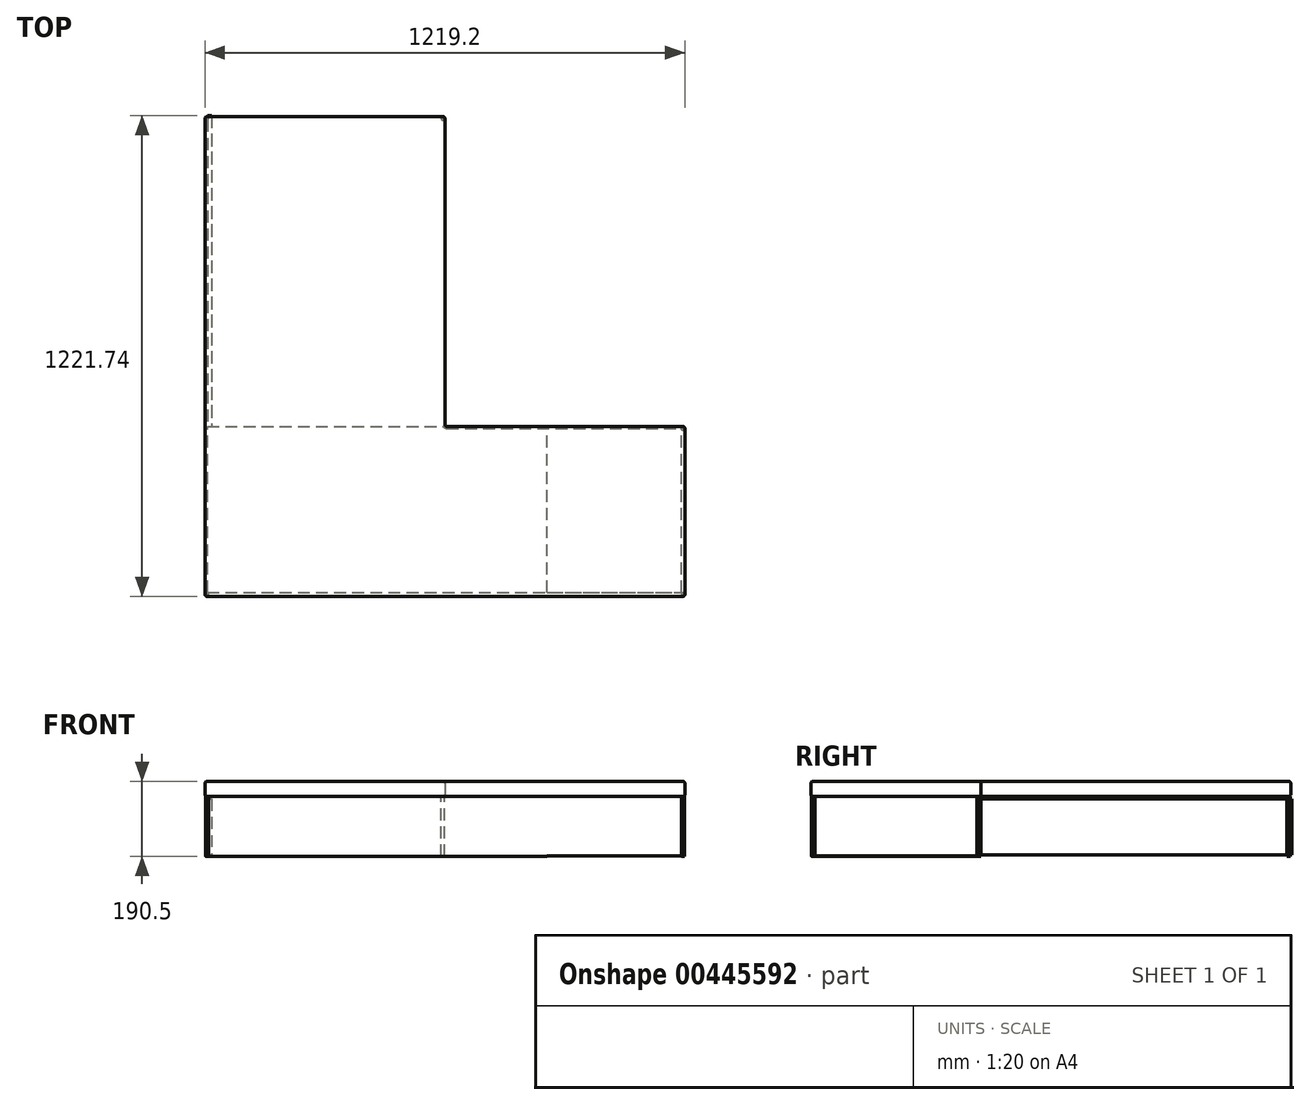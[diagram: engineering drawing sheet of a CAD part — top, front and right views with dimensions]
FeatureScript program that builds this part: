
annotation { "Feature Type Name" : "Feature", "Feature Type Description" : "" }
export const myFeature = defineFeature(function(context is Context, id is Id, definition is map)
    precondition{}
    {
        {
            var Q0;
            Q0=qCreatedBy(makeId("Top.planeOp"),FACE);
            var sketch = newSketch(context, id + "F0", { "sketchPlane" : qUnion([Q0])});
            skLineSegment(sketch, "E0.bottom", {"start": v(0, 0) * mm, "end": v(-609.6, 0) * mm});
            skLineSegment(sketch, "E0.top", {"start": v(0, 787.4) * mm, "end": v(-609.6, 787.4) * mm});
            skLineSegment(sketch, "E0.left", {"start": v(0, 0) * mm, "end": v(0, 787.4) * mm});
            skLineSegment(sketch, "E0.right", {"start": v(-609.6, 0) * mm, "end": v(-609.6, 787.4) * mm});
            skLineSegment(sketch, "E1.top", {"start": v(0, -431.8) * mm, "end": v(-609.6, -431.8) * mm});
            skLineSegment(sketch, "E1.left", {"start": v(0, 0) * mm, "end": v(0, -431.8) * mm});
            skLineSegment(sketch, "E1.right", {"start": v(-609.6, 0) * mm, "end": v(-609.6, -431.8) * mm});
            skLineSegment(sketch, "E2.bottom", {"start": v(0, -431.8) * mm, "end": v(609.6, -431.8) * mm});
            skLineSegment(sketch, "E2.top", {"start": v(0, 0) * mm, "end": v(609.6, 0) * mm});
            skLineSegment(sketch, "E2.left", {"start": v(0, -431.8) * mm, "end": v(0, 0) * mm});
            skLineSegment(sketch, "E2.right", {"start": v(609.6, -431.8) * mm, "end": v(609.6, 0) * mm});
            skSolve(sketch);
        }
        {
            var Q0;
            Q0 = qSketchRegion(id + "F0", true);
            extrude(context, id + "F1", {"entities" : qUnion([Q0]), "depth" : 38.1 * mm});
        }
        {
            var Q0;
            Q0=makeQuery(id+"F1.opExtrude","CAP_EDGE",EDGE,{"disambiguationData":[OSD([sQuery(id+"F0.wireOp",EDGE,"E1.top"),sQuery(id+"F0.wireOp",EDGE,"E2.bottom")])],"isStart":false});
            var Q1;
            Q1=makeQuery(id+"F1.opExtrude","SWEPT_EDGE",EDGE,{"disambiguationData":[OSD([sQuery(id+"F0.wireOp",EDGE,"E2.bottom"),sQuery(id+"F0.wireOp",EDGE,"E2.right")])]});
            var Q2;
            Q2=makeQuery(id+"F1.opExtrude","CAP_EDGE",EDGE,{"disambiguationData":[OSD([sQuery(id+"F0.wireOp",EDGE,"E2.right")])],"isStart":false});
            var Q3;
            Q3=makeQuery(id+"F1.opExtrude","CAP_EDGE",EDGE,{"disambiguationData":[OSD([sQuery(id+"F0.wireOp",EDGE,"E2.top")])],"isStart":false});
            var Q4;
            Q4=makeQuery(id+"F1.opExtrude","CAP_EDGE",EDGE,{"disambiguationData":[OSD([sQuery(id+"F0.wireOp",EDGE,"E0.left")])],"isStart":false});
            var Q5;
            Q5=makeQuery(id+"F1.opExtrude","CAP_EDGE",EDGE,{"disambiguationData":[OSD([sQuery(id+"F0.wireOp",EDGE,"E0.right"),sQuery(id+"F0.wireOp",EDGE,"E1.right")])],"isStart":false});
            var Q6;
            Q6=makeQuery(id+"F1.opExtrude","CAP_EDGE",EDGE,{"disambiguationData":[OSD([sQuery(id+"F0.wireOp",EDGE,"E0.top")])],"isStart":false});
            var Q7;
            Q7=makeQuery(id+"F1.opExtrude","CAP_EDGE",EDGE,{"disambiguationData":[OSD([sQuery(id+"F0.wireOp",EDGE,"E0.left")])],"isStart":true});
            var Q8;
            Q8=makeQuery(id+"F1.opExtrude","SWEPT_EDGE",EDGE,{"disambiguationData":[OSD([sQuery(id+"F0.wireOp",EDGE,"E2.top"),sQuery(id+"F0.wireOp",EDGE,"E2.right")])]});
            var Q9;
            Q9=makeQuery(id+"F1.opExtrude","CAP_EDGE",EDGE,{"disambiguationData":[OSD([sQuery(id+"F0.wireOp",EDGE,"E2.top")])],"isStart":true});
            var Q10;
            Q10=makeQuery(id+"F1.opExtrude","SWEPT_EDGE",EDGE,{"disambiguationData":[OSD([sQuery(id+"F0.wireOp",EDGE,"E0.left"),sQuery(id+"F0.wireOp",EDGE,"E0.bottom"),sQuery(id+"F0.wireOp",EDGE,"E2.top"),sQuery(id+"F0.wireOp",EDGE,"E2.left")])]});
            var Q11;
            Q11=makeQuery(id+"F1.opExtrude","SWEPT_FACE",FACE,{"disambiguationData":[OSD([sQuery(id+"F0.wireOp",EDGE,"E2.right")])]});
            var Q12;
            Q12=makeQuery(id+"F1.opExtrude","SWEPT_EDGE",EDGE,{"disambiguationData":[OSD([sQuery(id+"F0.wireOp",EDGE,"E0.top"),sQuery(id+"F0.wireOp",EDGE,"E0.left")])]});
            var Q13;
            Q13=makeQuery(id+"F1.opExtrude","CAP_EDGE",EDGE,{"disambiguationData":[OSD([sQuery(id+"F0.wireOp",EDGE,"E0.top")])],"isStart":true});
            var Q14;
            Q14=makeQuery(id+"F1.opExtrude","SWEPT_FACE",FACE,{"disambiguationData":[OSD([sQuery(id+"F0.wireOp",EDGE,"E0.right"),sQuery(id+"F0.wireOp",EDGE,"E1.right")])]});
            var Q15;
            Q15=makeQuery(id+"F1.opExtrude","CAP_EDGE",EDGE,{"disambiguationData":[OSD([sQuery(id+"F0.wireOp",EDGE,"E1.top"),sQuery(id+"F0.wireOp",EDGE,"E2.bottom")])],"isStart":true});
            fillet(context, id + "F2", {"entities" : qUnion([Q0, Q1, Q2, Q3, Q4, Q5, Q6, Q7, Q8, Q9, Q10, Q11, Q12, Q13, Q14, Q15]), "radius" : 5.08 * mm, "tangentPropagation" : true, "allowEdgeOverflow" : false});
        }
        {
            var Q0;
            Q0=makeQuery(id+"F1.opExtrude","CAP_FACE",FACE,{"disambiguationData":[OSD([sQuery(id+"F0.wireOp",EDGE,"E0.top"),sQuery(id+"F0.wireOp",EDGE,"E0.left"),sQuery(id+"F0.wireOp",EDGE,"E0.right"),sQuery(id+"F0.wireOp",EDGE,"E1.top"),sQuery(id+"F0.wireOp",EDGE,"E1.right"),sQuery(id+"F0.wireOp",EDGE,"E2.bottom"),sQuery(id+"F0.wireOp",EDGE,"E2.top"),sQuery(id+"F0.wireOp",EDGE,"E2.right")])],"isStart":true});
            var sketch = newSketch(context, id + "F3", { "sketchPlane" : qUnion([Q0])});
            skCircle(sketch, "E3", {"center": v(-604.52, -782.32) * mm, "radius": 3.88 * mm});
            skSolve(sketch);
        }
        {
            var Q0;
            Q0 = qSketchRegion(id + "F3", true);
            extrude(context, id + "F4", {"entities" : qUnion([Q0]), "operationType" : NewBodyOperationType.ADD, "depth" : 152.4 * mm});
        }
        {
            var Q0;
            Q0=makeQuery(id+"F1.opExtrude","CAP_FACE",FACE,{"disambiguationData":[OSD([sQuery(id+"F0.wireOp",EDGE,"E0.top"),sQuery(id+"F0.wireOp",EDGE,"E0.left"),sQuery(id+"F0.wireOp",EDGE,"E0.right"),sQuery(id+"F0.wireOp",EDGE,"E1.top"),sQuery(id+"F0.wireOp",EDGE,"E1.right"),sQuery(id+"F0.wireOp",EDGE,"E2.bottom"),sQuery(id+"F0.wireOp",EDGE,"E2.top"),sQuery(id+"F0.wireOp",EDGE,"E2.right")])],"isStart":true});
            var sketch = newSketch(context, id + "F5", { "sketchPlane" : qUnion([Q0])});
            skCircle(sketch, "E4", {"center": v(-604.52, 426.72) * mm, "radius": 3.78 * mm});
            skSolve(sketch);
        }
        {
            var Q0;
            Q0 = qSketchRegion(id + "F5", true);
            extrude(context, id + "F6", {"entities" : qUnion([Q0]), "operationType" : NewBodyOperationType.ADD, "depth" : 152.4 * mm});
        }
        {
            var Q0;
            Q0=makeQuery(id+"F1.opExtrude","CAP_FACE",FACE,{"disambiguationData":[OSD([sQuery(id+"F0.wireOp",EDGE,"E0.top"),sQuery(id+"F0.wireOp",EDGE,"E0.left"),sQuery(id+"F0.wireOp",EDGE,"E0.right"),sQuery(id+"F0.wireOp",EDGE,"E1.top"),sQuery(id+"F0.wireOp",EDGE,"E1.right"),sQuery(id+"F0.wireOp",EDGE,"E2.bottom"),sQuery(id+"F0.wireOp",EDGE,"E2.top"),sQuery(id+"F0.wireOp",EDGE,"E2.right")])],"isStart":true});
            var sketch = newSketch(context, id + "F7", { "sketchPlane" : qUnion([Q0])});
            skCircle(sketch, "E5", {"center": v(604.52, 426.72) * mm, "radius": 3.99 * mm});
            skSolve(sketch);
        }
        {
            var Q0;
            Q0 = qSketchRegion(id + "F7", true);
            extrude(context, id + "F8", {"entities" : qUnion([Q0]), "operationType" : NewBodyOperationType.ADD, "depth" : 152.4 * mm});
        }
        {
            var Q0;
            Q0=makeQuery(id+"F1.opExtrude","CAP_FACE",FACE,{"disambiguationData":[OSD([sQuery(id+"F0.wireOp",EDGE,"E0.top"),sQuery(id+"F0.wireOp",EDGE,"E0.left"),sQuery(id+"F0.wireOp",EDGE,"E0.right"),sQuery(id+"F0.wireOp",EDGE,"E1.top"),sQuery(id+"F0.wireOp",EDGE,"E1.right"),sQuery(id+"F0.wireOp",EDGE,"E2.bottom"),sQuery(id+"F0.wireOp",EDGE,"E2.top"),sQuery(id+"F0.wireOp",EDGE,"E2.right")])],"isStart":true});
            var sketch = newSketch(context, id + "F9", { "sketchPlane" : qUnion([Q0])});
            skCircle(sketch, "E6", {"center": v(604.52, 5.08) * mm, "radius": 4.25 * mm});
            skSolve(sketch);
        }
        {
            var Q0;
            Q0 = qSketchRegion(id + "F9", true);
            extrude(context, id + "F10", {"entities" : qUnion([Q0]), "operationType" : NewBodyOperationType.ADD, "depth" : 152.4 * mm});
        }
        {
            var Q0;
            Q0=makeQuery(id+"F1.opExtrude","CAP_FACE",FACE,{"disambiguationData":[OSD([sQuery(id+"F0.wireOp",EDGE,"E0.top"),sQuery(id+"F0.wireOp",EDGE,"E0.left"),sQuery(id+"F0.wireOp",EDGE,"E0.right"),sQuery(id+"F0.wireOp",EDGE,"E1.top"),sQuery(id+"F0.wireOp",EDGE,"E1.right"),sQuery(id+"F0.wireOp",EDGE,"E2.bottom"),sQuery(id+"F0.wireOp",EDGE,"E2.top"),sQuery(id+"F0.wireOp",EDGE,"E2.right")])],"isStart":true});
            var sketch = newSketch(context, id + "F11", { "sketchPlane" : qUnion([Q0])});
            skCircle(sketch, "E7", {"center": v(-5.08, -782.32) * mm, "radius": 4.3 * mm});
            skSolve(sketch);
        }
        {
            var Q0;
            Q0 = qSketchRegion(id + "F11", true);
            extrude(context, id + "F12", {"entities" : qUnion([Q0]), "operationType" : NewBodyOperationType.ADD, "depth" : 152.4 * mm});
        }
        {
            var Q0;
            Q0=qCreatedBy(makeId("Front.planeOp"),FACE);
            var sketch = newSketch(context, id + "F13", { "sketchPlane" : qUnion([Q0])});
            skLineSegment(sketch, "E8.bottom", {"start": v(0, 0) * mm, "end": v(600.76, 0) * mm});
            skLineSegment(sketch, "E8.top", {"start": v(0, -151.17) * mm, "end": v(600.76, -151.17) * mm});
            skLineSegment(sketch, "E8.left", {"start": v(0, 0) * mm, "end": v(0, -151.17) * mm});
            skLineSegment(sketch, "E8.right", {"start": v(600.76, 0) * mm, "end": v(600.76, -151.17) * mm});
            skSolve(sketch);
        }
        {
            var Q0;
            Q0=qCreatedBy(makeId("Front.planeOp"),FACE);
            var sketch = newSketch(context, id + "F14", { "sketchPlane" : qUnion([Q0])});
            skLineSegment(sketch, "E9.bottom", {"start": v(-603.5, 0) * mm, "end": v(259.38, 0) * mm});
            skLineSegment(sketch, "E9.top", {"start": v(-603.5, -152.4) * mm, "end": v(259.38, -152.4) * mm});
            skLineSegment(sketch, "E9.left", {"start": v(-603.5, 0) * mm, "end": v(-603.5, -152.4) * mm});
            skLineSegment(sketch, "E9.right", {"start": v(259.38, 0) * mm, "end": v(259.38, -152.4) * mm});
            skSolve(sketch);
        }
        {
            var Q0;
            Q0=makeQuery(id+"F13.imprint","IMPRINT",FACE,{"disambiguationData":[TD([[makeQuery(id+"F13.imprint","IMPRINT",EDGE,{"derivedFrom":sQuery(id+"F13.wireOp",EDGE,"E8.bottom")}),-1.0]])]});
            extrude(context, id + "F15", {"entities" : qUnion([Q0]), "operationType" : NewBodyOperationType.ADD, "depth" : 421.64 * mm});
        }
        {
            var Q0;
            Q0=makeQuery(id+"F14.imprint","IMPRINT",FACE,{"disambiguationData":[TD([[makeQuery(id+"F14.imprint","IMPRINT",EDGE,{"derivedFrom":sQuery(id+"F14.wireOp",EDGE,"E9.bottom")}),-1.0]])]});
            extrude(context, id + "F16", {"entities" : qUnion([Q0]), "operationType" : NewBodyOperationType.ADD, "depth" : 421.64 * mm});
        }
        {
            var Q0;
            Q0=qCreatedBy(makeId("Front.planeOp"),FACE);
            var sketch = newSketch(context, id + "F17", { "sketchPlane" : qUnion([Q0])});
            skLineSegment(sketch, "E10.bottom", {"start": v(-603.36, -6.7) * mm, "end": v(-592.29, -6.7) * mm});
            skLineSegment(sketch, "E10.top", {"start": v(-603.36, -149.27) * mm, "end": v(-592.29, -149.27) * mm});
            skLineSegment(sketch, "E10.left", {"start": v(-603.36, -6.7) * mm, "end": v(-603.36, -149.27) * mm});
            skLineSegment(sketch, "E10.right", {"start": v(-592.29, -6.7) * mm, "end": v(-592.29, -149.27) * mm});
            skSolve(sketch);
        }
        {
            var Q0;
            Q0=makeQuery(id+"F17.imprint","IMPRINT",FACE,{"disambiguationData":[TD([[makeQuery(id+"F17.imprint","IMPRINT",EDGE,{"derivedFrom":sQuery(id+"F17.wireOp",EDGE,"E10.bottom")}),-1.0]])]});
            extrude(context, id + "F18", {"entities" : qUnion([Q0]), "operationType" : NewBodyOperationType.ADD, "oppositeDirection" : true, "depth" : 789.94 * mm});
        }
    });
